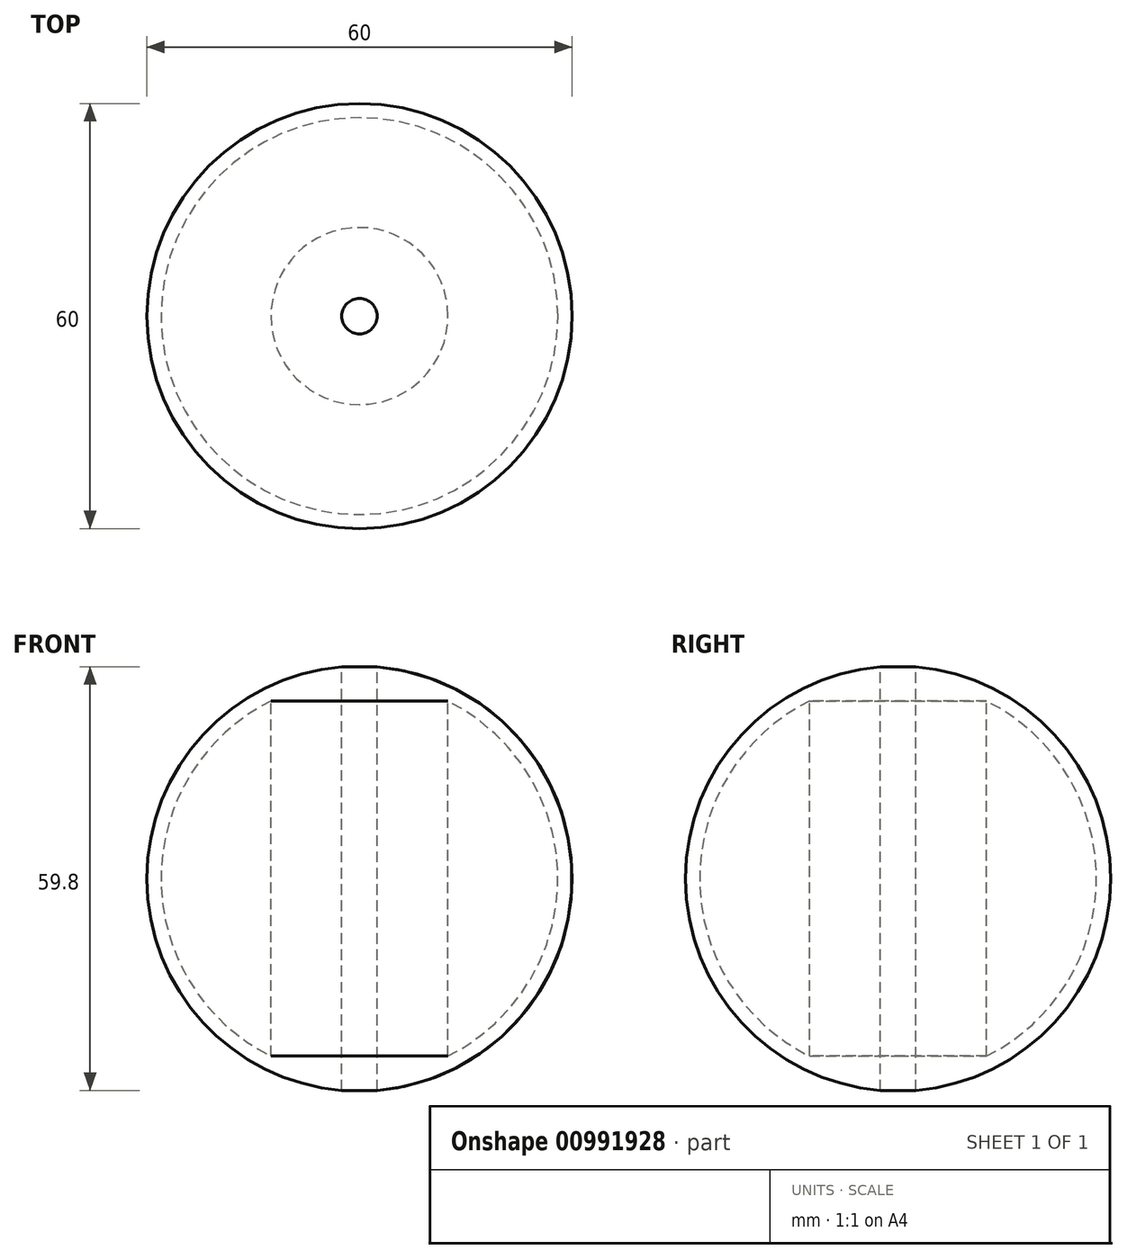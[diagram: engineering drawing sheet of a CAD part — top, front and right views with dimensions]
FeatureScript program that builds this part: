
annotation { "Feature Type Name" : "Feature", "Feature Type Description" : "" }
export const myFeature = defineFeature(function(context is Context, id is Id, definition is map)
    precondition{}
    {
        {
            var Q0;
            Q0=qCreatedBy(makeId("Front.planeOp"),FACE);
            var sketch = newSketch(context, id + "F0", { "sketchPlane" : qUnion([Q0])});
            skCircle(sketch, "E0", {"center": v(0, 0) * mm, "radius": 30 * mm});
            skCircle(sketch, "E1.0", {"center": v(0, 0) * mm, "radius": 28 * mm});
            skLineSegment(sketch, "E2", {"start": v(0, 37.54) * mm, "end": v(0, -35.06) * mm, "construction": true});
            skLineSegment(sketch, "E3", {"start": v(-2.5, 29.9) * mm, "end": v(-2.5, -29.9) * mm});
            skLineSegment(sketch, "E4", {"start": v(2.5, 29.9) * mm, "end": v(2.5, -29.9) * mm});
            skLineSegment(sketch, "E5", {"start": v(-12.5, 25.05) * mm, "end": v(-12.5, -25.05) * mm});
            skLineSegment(sketch, "E6", {"start": v(12.5, 25.05) * mm, "end": v(12.5, -25.05) * mm});
            skSolve(sketch);
        }
        {
            var Q0;
            {var subQ0=sQuery(id+"F0.wireOp",EDGE,"E3");var subQ1=sQuery(id+"F0.wireOp",EDGE,"E0");var subQ2=makeQuery(id+"F0.imprint","INTERSECT",VERTEX,{"disambiguationData":[OD(0.0)],"derivedFrom":[subQ1,subQ0]});Q0=makeQuery(id+"F0.imprint","IMPRINT",FACE,{"disambiguationData":[TD([[makeQuery(id+"F0.imprint","IMPRINT",EDGE,{"disambiguationData":[TD([[subQ2,-1.0]])],"derivedFrom":subQ1}),1.0]])]});}
            var Q1;
            {var subQ0=sQuery(id+"F0.wireOp",EDGE,"E5");Q1=makeQuery(id+"F0.imprint","IMPRINT",FACE,{"disambiguationData":[TD([[makeQuery(id+"F0.imprint","IMPRINT",EDGE,{"derivedFrom":subQ0}),1.0]])]});}
            var Q2;
            Q2=sQuery(id+"F0.wireOp",EDGE,"E2");
            revolve(context, id + "F1", {"surfaceOperationType" : NewSurfaceOperationType.NEW, "entities" : qUnion([Q0, Q1]), "axis" : qUnion([Q2]), "revolveType" : RevolveType.FULL});
        }
    });
